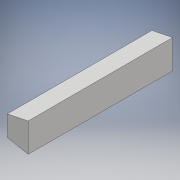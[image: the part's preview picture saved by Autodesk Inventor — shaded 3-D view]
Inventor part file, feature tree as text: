
AUTODESK INVENTOR PART (.ipt)
format: ipt  version: 2017 (Build 210142000, 142)  size: 90,624 bytes
history: native  units: mm
features: extrude x1, sketch x1
ambient origin geometry x8: Origin, YZ Plane, XZ Plane, XY Plane, X Axis, Y Axis, Z Axis, Center Point
bodies: Solid1 (feature_tree)
feature tree (2):
  extrude  "Extrusion1"  Depth=5.0mm
  sketch  "Sketch1"  dims[d0=7.0mm d1=5.0mm d2=1.0mm d3=35.0mm d4=0.0mm d5=5.0mm]
